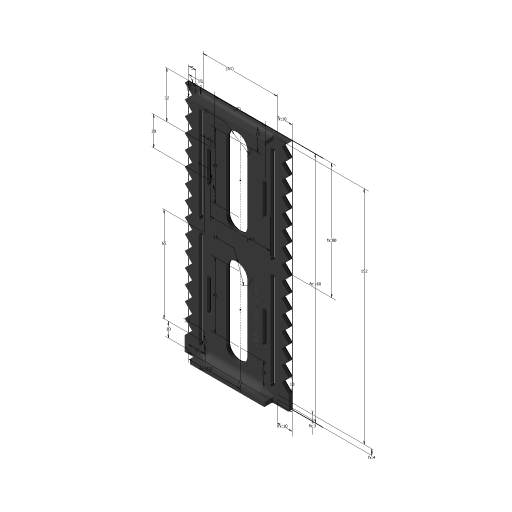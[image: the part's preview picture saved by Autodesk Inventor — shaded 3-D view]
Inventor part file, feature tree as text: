
AUTODESK INVENTOR PART (.ipt)
format: ipt  version: 2023 (Build 270158000, 158)  size: 602,112 bytes
history: native  units: mm
features: extrude x5, sketch x2, fillet x2
ambient origin geometry x8: Origin, YZ Plane, XZ Plane, XY Plane, X Axis, Y Axis, Z Axis, Center Point
bodies: Solid1 (feature_tree)
feature tree (9):
  sketch  "Sketch1"  dims[d0=71.0mm d1=160.0mm]
  extrude  "Extrusion1"  Depth=160.0mm
  extrude  "Extrusion2"  Depth=5.0mm
  fillet  "Fillet1"  Radius=160.0mm
  extrude  "Extrusion3"  Depth=35.5mm
  extrude  "Extrusion4"  Depth=10.0mm
  fillet  "Fillet2"  Radius=10.0mm
  extrude  "Extrusion5"  Depth=3.0mm
  sketch  "Sketch2"  dims[d2=45.0deg d3=5.0mm d4=160.0mm d6=10.0mm d7=10.0mm d9=10.0mm d11=35.5mm d12=10.0mm d13=10.0mm d14=3.0mm d15=10.0mm d16=3.0mm d17=152.0mm d19=4.0mm d20=3.2mm d21=11.0mm d22=10.0mm d24=51.0mm d25=3.0mm d26=4.0mm d27=32.0mm d28=20.0mm d29=35.0mm d30=41.0mm d31=2.5mm d32=0.0mm d33=9.0mm d34=0.0mm d35=3.0mm d36=45.0mm d37=15.0mm d38=15.0mm d39=45.0mm d40=15.0mm d41=15.0mm d42=0.0mm d43=0.0mm d44=65.0mm d45=80.0mm d46=0.0mm d47=0.0mm d48=20.0mm d50=10.0mm d51=10.0mm d53=10.0mm d55=0.0mm d56=0.0mm d57=5.0mm d58=2.0mm d59=5.0mm d60=8.0mm d61=0.0mm d62=0.0mm d63=5.0mm d64=2.0mm d65=5.0mm d66=8.0mm d67=1.0mm d68=0.0mm]
